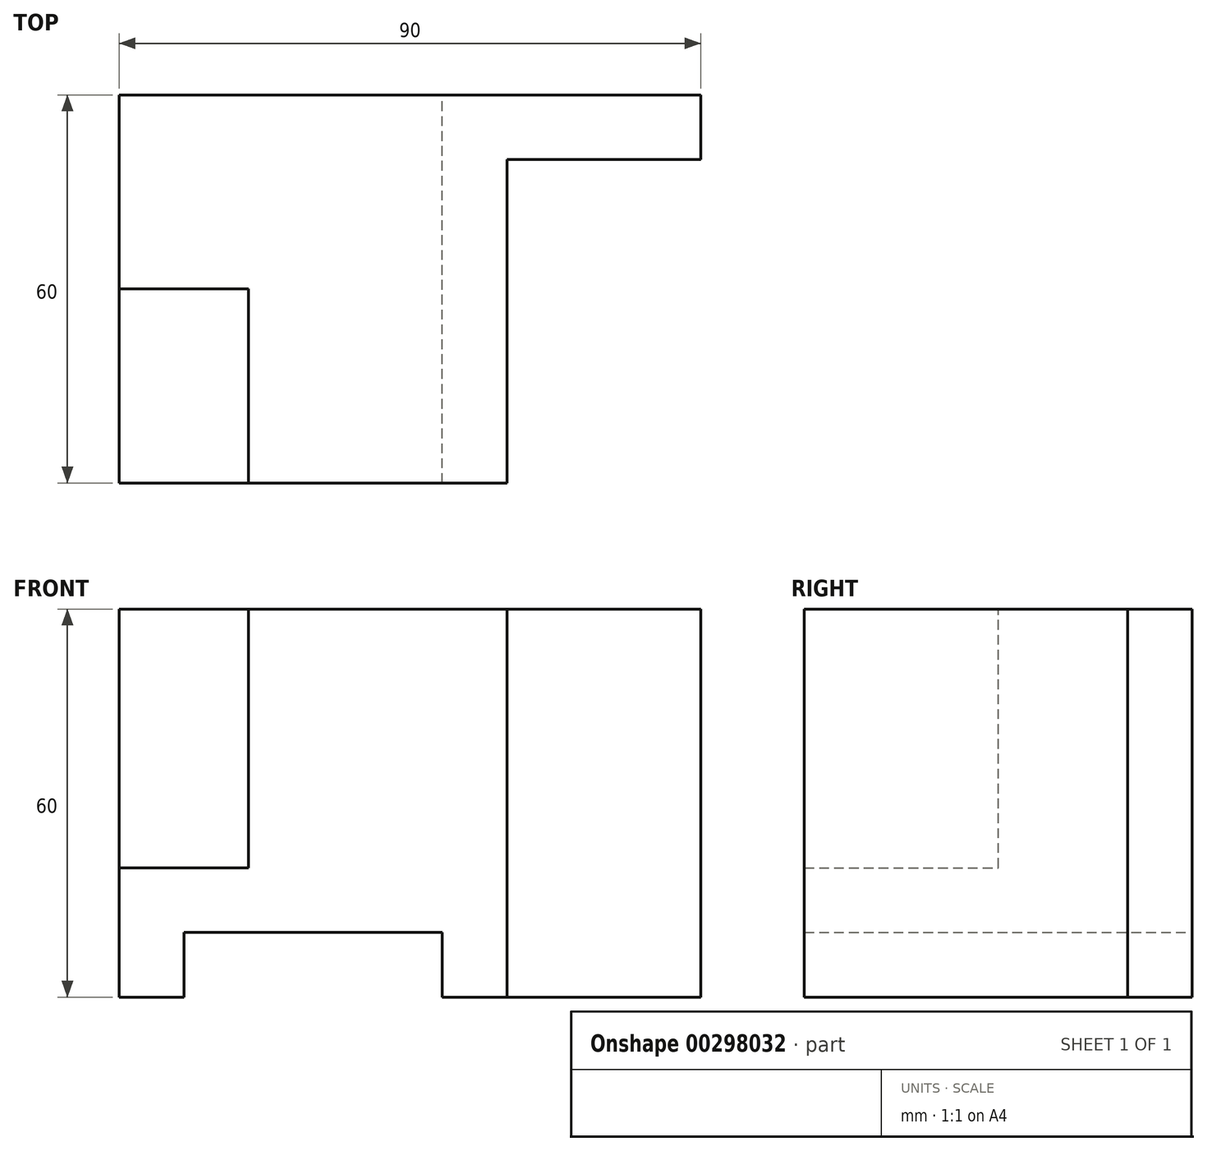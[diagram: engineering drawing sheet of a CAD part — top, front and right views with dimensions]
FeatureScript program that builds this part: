
annotation { "Feature Type Name" : "Feature", "Feature Type Description" : "" }
export const myFeature = defineFeature(function(context is Context, id is Id, definition is map)
    precondition{}
    {
        {
            var Q0;
            Q0=qCreatedBy(makeId("Front.planeOp"),FACE);
            var sketch = newSketch(context, id + "F0", { "sketchPlane" : qUnion([Q0])});
            skLineSegment(sketch, "E0.bottom", {"start": v(-43.5, 32.32) * mm, "end": v(46.5, 32.32) * mm});
            skLineSegment(sketch, "E0.top", {"start": v(-43.5, -27.68) * mm, "end": v(46.5, -27.68) * mm});
            skLineSegment(sketch, "E0.left", {"start": v(-43.5, 32.32) * mm, "end": v(-43.5, -27.68) * mm});
            skLineSegment(sketch, "E0.right", {"start": v(46.5, 32.32) * mm, "end": v(46.5, -27.68) * mm});
            skSolve(sketch);
        }
        {
            var Q0;
            Q0=makeQuery(id+"F0.imprint","IMPRINT",FACE,{"disambiguationData":[TD([[makeQuery(id+"F0.imprint","IMPRINT",EDGE,{"derivedFrom":sQuery(id+"F0.wireOp",EDGE,"E0.bottom")}),-1.0]])]});
            extrude(context, id + "F1", {"entities" : qUnion([Q0]), "depth" : 60 * mm});
        }
        {
            var Q0;
            Q0=makeQuery(id+"F1.opExtrude","SWEPT_FACE",FACE,{"disambiguationData":[OSD([sQuery(id+"F0.wireOp",EDGE,"E0.bottom")])]});
            var sketch = newSketch(context, id + "F2", { "sketchPlane" : qUnion([Q0])});
            skLineSegment(sketch, "E1.bottom", {"start": v(46.5, -60) * mm, "end": v(16.5, -60) * mm});
            skLineSegment(sketch, "E1.top", {"start": v(46.5, -10) * mm, "end": v(16.5, -10) * mm});
            skLineSegment(sketch, "E1.left", {"start": v(46.5, -60) * mm, "end": v(46.5, -10) * mm});
            skLineSegment(sketch, "E1.right", {"start": v(16.5, -60) * mm, "end": v(16.5, -10) * mm});
            skSolve(sketch);
        }
        {
            var Q0;
            Q0=makeQuery(id+"F2.imprint","IMPRINT",FACE,{"disambiguationData":[TD([[makeQuery(id+"F2.imprint","IMPRINT",EDGE,{"derivedFrom":sQuery(id+"F2.wireOp",EDGE,"E1.bottom")}),1.0]])]});
            extrude(context, id + "F3", {"entities" : qUnion([Q0]), "operationType" : NewBodyOperationType.REMOVE, "oppositeDirection" : true, "depth" : 60 * mm});
        }
        {
            var Q0;
            Q0=makeQuery(id+"F1.opExtrude","SWEPT_FACE",FACE,{"disambiguationData":[OSD([sQuery(id+"F0.wireOp",EDGE,"E0.bottom")])]});
            var sketch = newSketch(context, id + "F4", { "sketchPlane" : qUnion([Q0])});
            skLineSegment(sketch, "E2.bottom", {"start": v(-43.5, -60) * mm, "end": v(-23.5, -60) * mm});
            skLineSegment(sketch, "E2.top", {"start": v(-43.5, -30) * mm, "end": v(-23.5, -30) * mm});
            skLineSegment(sketch, "E2.left", {"start": v(-43.5, -60) * mm, "end": v(-43.5, -30) * mm});
            skLineSegment(sketch, "E2.right", {"start": v(-23.5, -60) * mm, "end": v(-23.5, -30) * mm});
            skSolve(sketch);
        }
        {
            var Q0;
            Q0=makeQuery(id+"F4.imprint","IMPRINT",FACE,{"disambiguationData":[TD([[makeQuery(id+"F4.imprint","IMPRINT",EDGE,{"derivedFrom":sQuery(id+"F4.wireOp",EDGE,"E2.bottom")}),1.0]])]});
            extrude(context, id + "F5", {"entities" : qUnion([Q0]), "operationType" : NewBodyOperationType.REMOVE, "oppositeDirection" : true, "depth" : 40 * mm});
        }
        {
            var Q0;
            Q0=makeQuery(id+"F1.opExtrude","SWEPT_FACE",FACE,{"disambiguationData":[OSD([sQuery(id+"F0.wireOp",EDGE,"E0.top")])]});
            var sketch = newSketch(context, id + "F6", { "sketchPlane" : qUnion([Q0])});
            skLineSegment(sketch, "E3.bottom", {"start": v(-33.5, 60) * mm, "end": v(6.5, 60) * mm});
            skLineSegment(sketch, "E3.top", {"start": v(-33.5, 0) * mm, "end": v(6.5, 0) * mm});
            skLineSegment(sketch, "E3.left", {"start": v(-33.5, 60) * mm, "end": v(-33.5, 0) * mm});
            skLineSegment(sketch, "E3.right", {"start": v(6.5, 60) * mm, "end": v(6.5, 0) * mm});
            skSolve(sketch);
        }
        {
            var Q0;
            Q0=makeQuery(id+"F6.imprint","IMPRINT",FACE,{"disambiguationData":[TD([[makeQuery(id+"F6.imprint","IMPRINT",EDGE,{"derivedFrom":sQuery(id+"F6.wireOp",EDGE,"E3.bottom")}),-1.0]])]});
            extrude(context, id + "F7", {"entities" : qUnion([Q0]), "operationType" : NewBodyOperationType.REMOVE, "oppositeDirection" : true, "depth" : 10 * mm});
        }
    });
